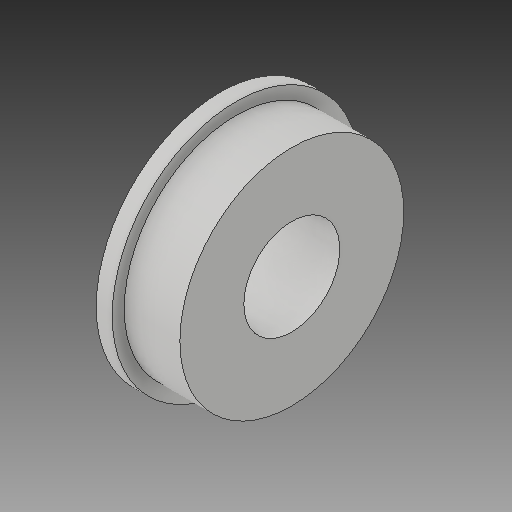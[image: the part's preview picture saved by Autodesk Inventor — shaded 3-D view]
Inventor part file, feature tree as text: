
AUTODESK INVENTOR PART (.ipt)
format: ipt  version: 2019 (Build 230136000, 136)  size: 128,000 bytes
history: native  units: in
note: dims shown in document units (in); Inventor stores cm internally (conversion verified against a paired STEP export)
features: revolve x1
ambient origin geometry x8: Origin, YZ Plane, XZ Plane, XY Plane, X Axis, Y Axis, Z Axis, Center Point
bodies: Solid1 (feature_tree)
feature tree (1):
  revolve  "Revolve1"  [1 undecoded]
note: 1 required parameter value undecoded (feature->parameter linkage not recoverable at this tier; creation-order binding heuristic only, values carry confidence <= 0.55)
